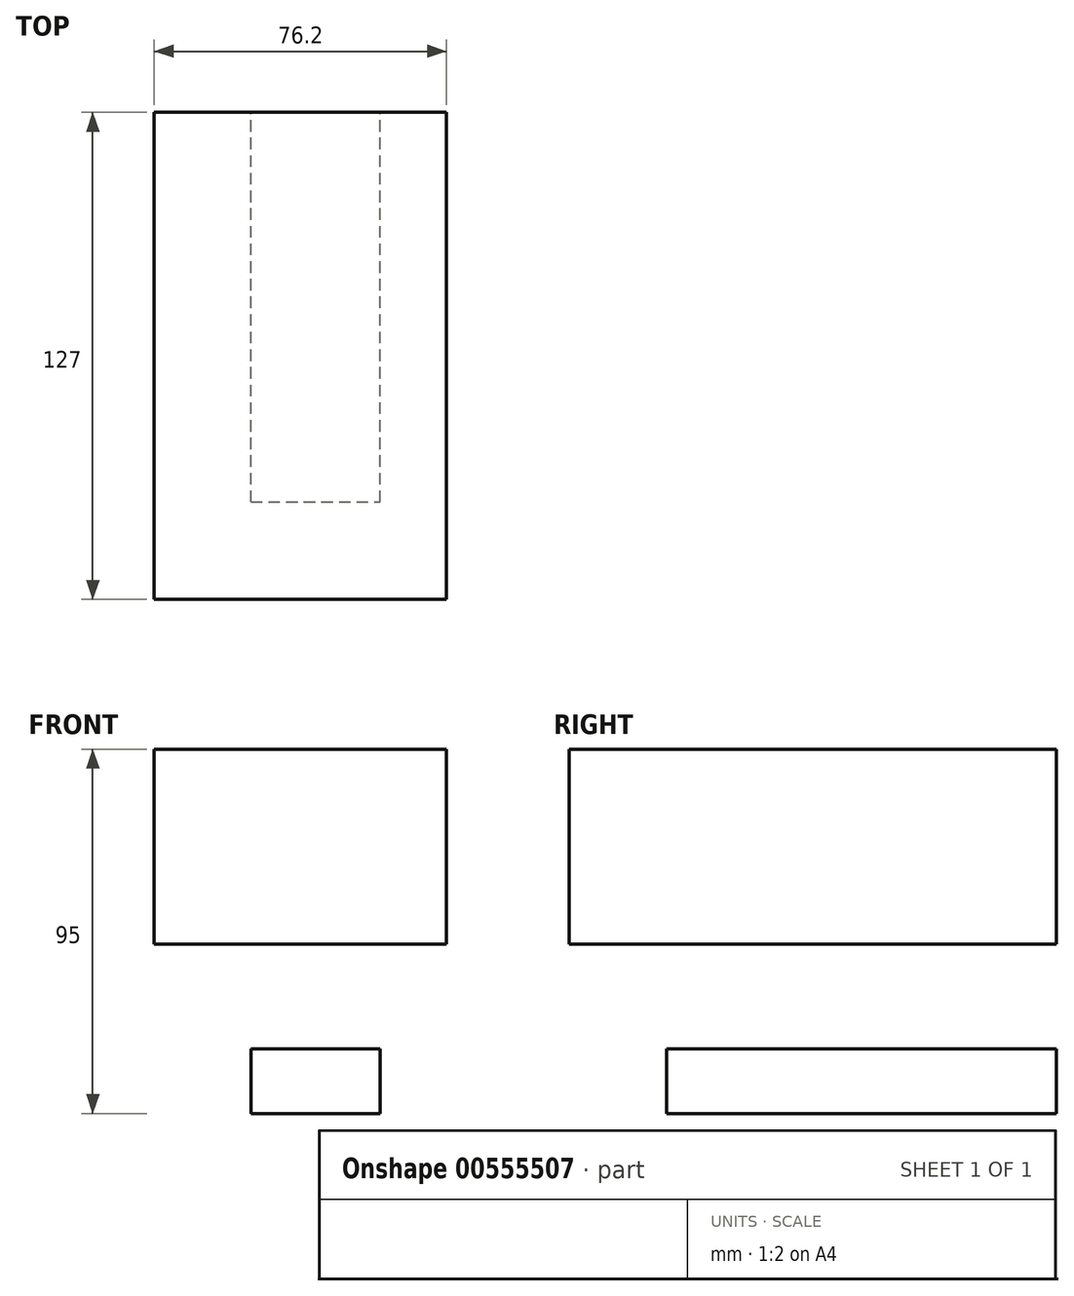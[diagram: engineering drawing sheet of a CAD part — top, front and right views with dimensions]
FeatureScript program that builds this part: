
annotation { "Feature Type Name" : "Feature", "Feature Type Description" : "" }
export const myFeature = defineFeature(function(context is Context, id is Id, definition is map)
    precondition{}
    {
        {
            var Q0;
            Q0=qCreatedBy(makeId("Front.planeOp"),FACE);
            var sketch = newSketch(context, id + "F0", { "sketchPlane" : qUnion([Q0])});
            skLineSegment(sketch, "E0.bottom", {"start": v(-67, 57.42) * mm, "end": v(9.2, 57.42) * mm});
            skLineSegment(sketch, "E0.top", {"start": v(-67, 6.62) * mm, "end": v(9.2, 6.62) * mm});
            skLineSegment(sketch, "E0.left", {"start": v(-67, 57.42) * mm, "end": v(-67, 6.62) * mm});
            skLineSegment(sketch, "E0.right", {"start": v(9.2, 57.42) * mm, "end": v(9.2, 6.62) * mm});
            skSolve(sketch);
        }
        {
            var Q0;
            Q0=makeQuery(id+"F0.imprint","IMPRINT",FACE,{"disambiguationData":[TD([[makeQuery(id+"F0.imprint","IMPRINT",EDGE,{"derivedFrom":sQuery(id+"F0.wireOp",EDGE,"E0.bottom")}),-1.0]])]});
            extrude(context, id + "F1", {"entities" : qUnion([Q0]), "depth" : 127 * mm, "offsetDistance" : 25.4 * mm});
        }
        {
            var Q0;
            Q0=qCreatedBy(makeId("Front.planeOp"),FACE);
            var sketch = newSketch(context, id + "F2", { "sketchPlane" : qUnion([Q0])});
            skLineSegment(sketch, "E1.bottom", {"start": v(-41.84, -20.72) * mm, "end": v(-8.13, -20.72) * mm});
            skLineSegment(sketch, "E1.top", {"start": v(-41.84, -37.58) * mm, "end": v(-8.13, -37.58) * mm});
            skLineSegment(sketch, "E1.left", {"start": v(-41.84, -20.72) * mm, "end": v(-41.84, -37.58) * mm});
            skLineSegment(sketch, "E1.right", {"start": v(-8.13, -20.72) * mm, "end": v(-8.13, -37.58) * mm});
            skSolve(sketch);
        }
        {
            var Q0;
            Q0=makeQuery(id+"F2.imprint","IMPRINT",FACE,{"disambiguationData":[TD([[makeQuery(id+"F2.imprint","IMPRINT",EDGE,{"derivedFrom":sQuery(id+"F2.wireOp",EDGE,"E1.bottom")}),-1.0]])]});
            extrude(context, id + "F3", {"entities" : qUnion([Q0]), "depth" : 101.6 * mm, "offsetDistance" : 25.4 * mm});
        }
    });
